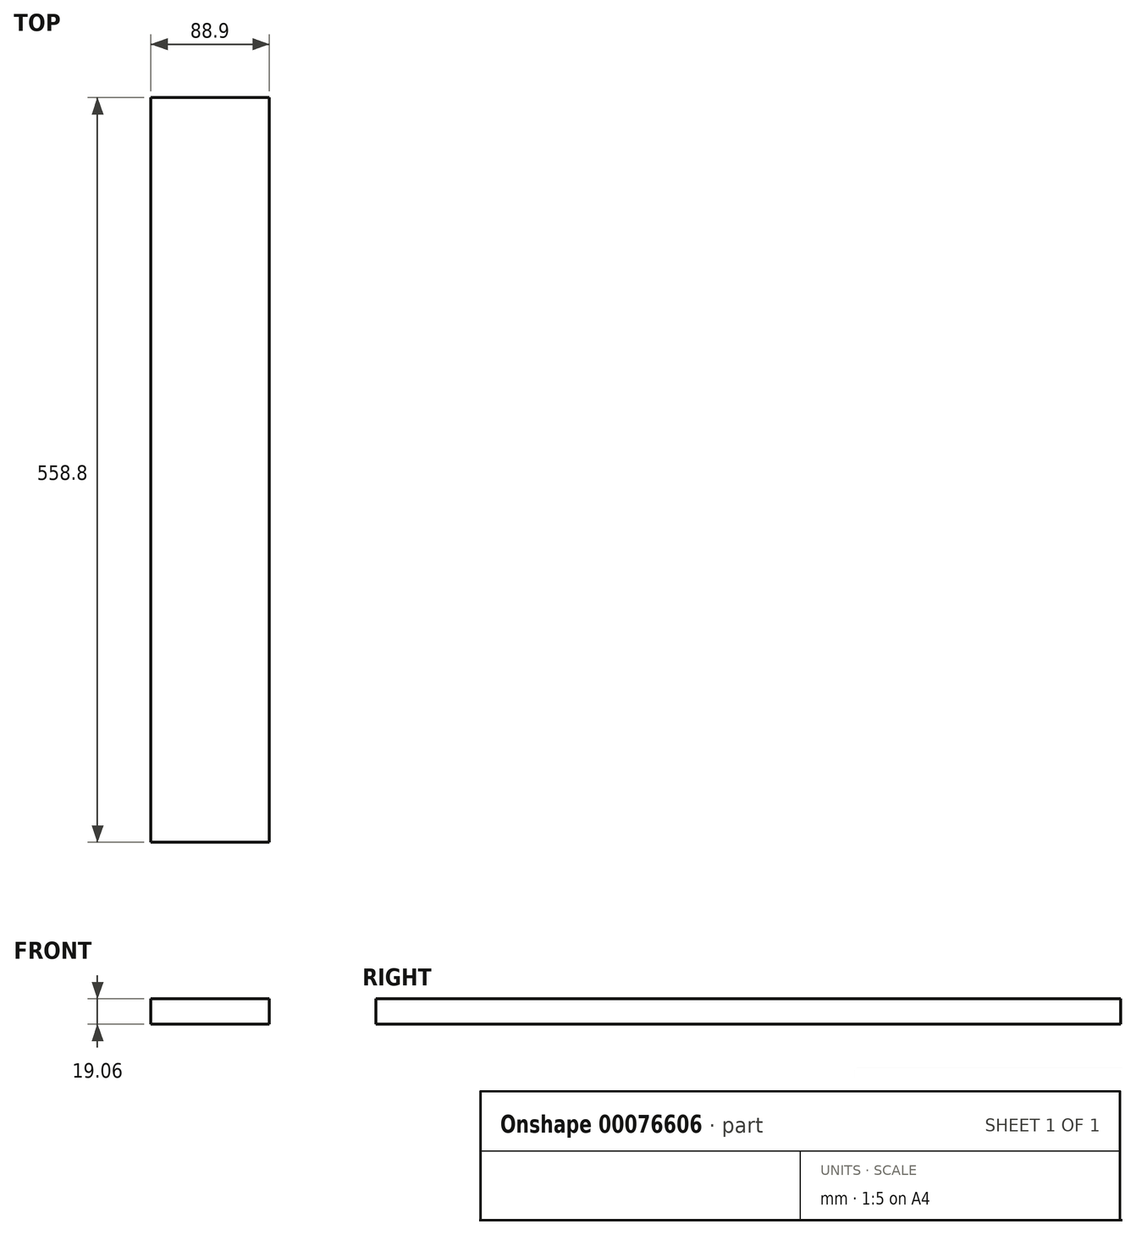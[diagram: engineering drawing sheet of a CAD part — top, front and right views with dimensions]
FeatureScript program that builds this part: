
annotation { "Feature Type Name" : "Feature", "Feature Type Description" : "" }
export const myFeature = defineFeature(function(context is Context, id is Id, definition is map)
    precondition{}
    {
        {
            var Q0;
            Q0=qCreatedBy(makeId("Front.planeOp"),FACE);
            var sketch = newSketch(context, id + "F0", { "sketchPlane" : qUnion([Q0])});
            skLineSegment(sketch, "E0.bottom", {"start": v(-44.45, 9.53) * mm, "end": v(44.45, 9.53) * mm});
            skLineSegment(sketch, "E0.top", {"start": v(-44.45, -9.52) * mm, "end": v(44.45, -9.52) * mm});
            skLineSegment(sketch, "E0.left", {"start": v(-44.45, 9.53) * mm, "end": v(-44.45, -9.52) * mm});
            skLineSegment(sketch, "E0.right", {"start": v(44.45, 9.53) * mm, "end": v(44.45, -9.52) * mm});
            skPoint(sketch, "E0.middle", {"position": v(0, 0) * mm});
            skSolve(sketch);
        }
        {
            var Q0;
            Q0=makeQuery(id+"F0.imprint","IMPRINT",FACE,{"disambiguationData":[TD([[makeQuery(id+"F0.imprint","IMPRINT",EDGE,{"derivedFrom":sQuery(id+"F0.wireOp",EDGE,"E0.bottom")}),-1.0]])]});
            extrude(context, id + "F1", {"entities" : qUnion([Q0]), "endBound" : BoundingType.SYMMETRIC, "oppositeDirection" : true, "depth" : 558.8 * mm});
        }
    });
